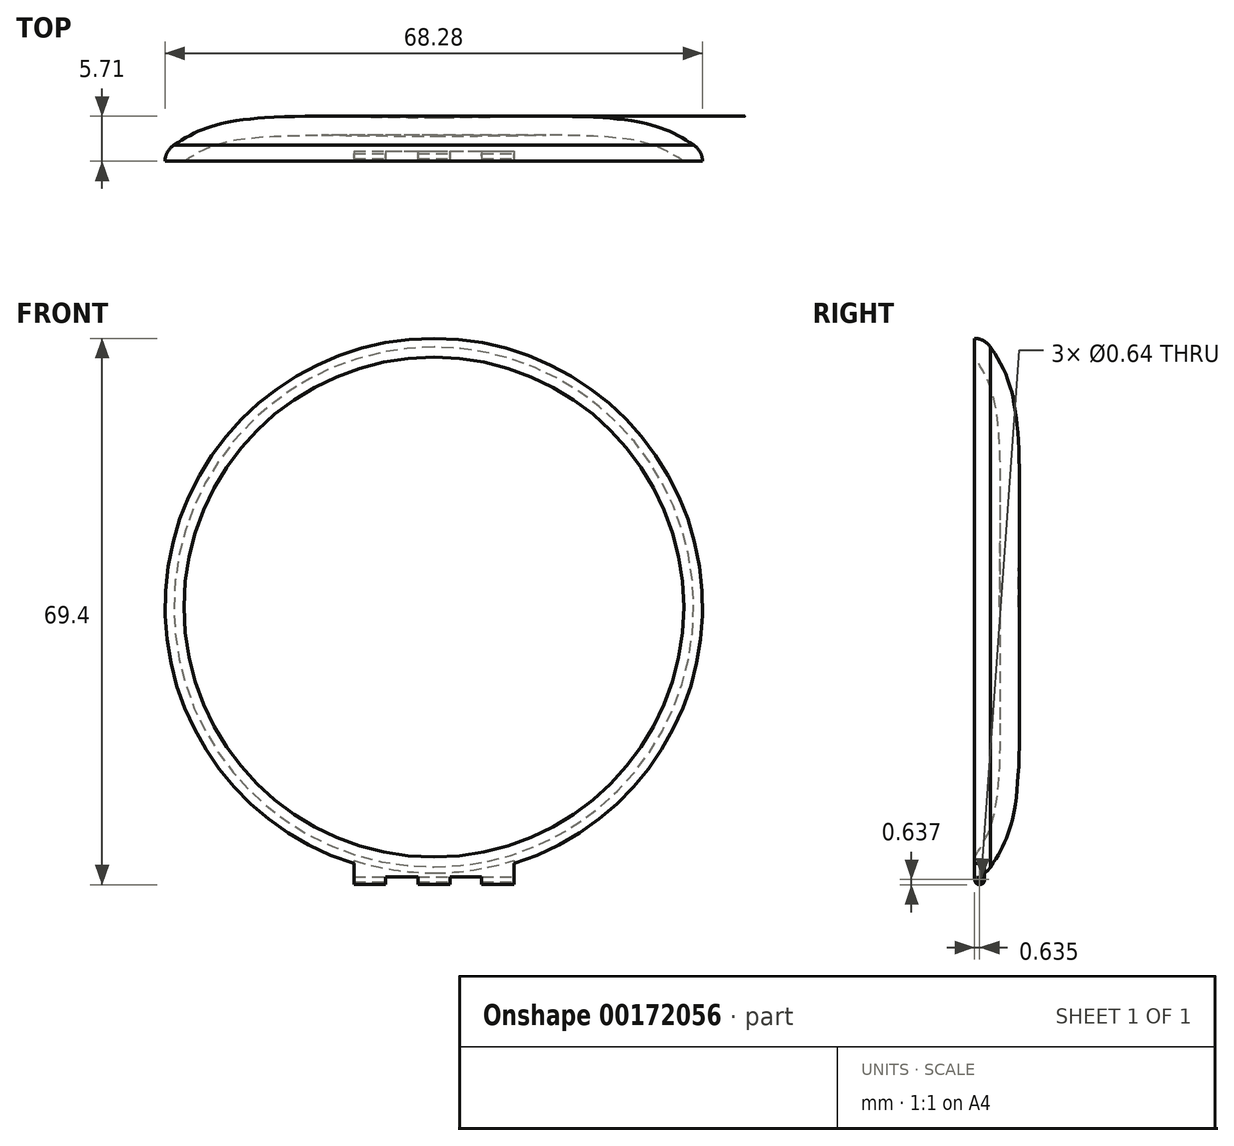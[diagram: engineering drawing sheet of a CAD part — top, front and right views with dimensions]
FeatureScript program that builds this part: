
annotation { "Feature Type Name" : "Feature", "Feature Type Description" : "" }
export const myFeature = defineFeature(function(context is Context, id is Id, definition is map)
    precondition{}
    {
        {
            var Q0;
            Q0=qCreatedBy(makeId("Right.planeOp"),FACE);
            var sketch = newSketch(context, id + "F0", { "sketchPlane" : qUnion([Q0])});
            skFitSpline(sketch, "E0", {"points": [v(3.18, 0) * mm, v(2.44, 26.5) * mm, v(0, 31.75) * mm], "startDerivative": vector(0, 46.41) * mm, "endDerivative": vector(-7.48, 11.96) * mm});
            skFitSpline(sketch, "E1.0", {"points": [v(5.56, 0) * mm, v(5.56, 1.92) * mm, v(5.6, 5.76) * mm, v(5.69, 11.37) * mm, v(5.7, 16.65) * mm, v(5.58, 20.62) * mm, v(5.36, 23.48) * mm, v(5.14, 25.12) * mm, v(4.92, 26.35) * mm, v(4.72, 27.23) * mm, v(4.5, 28.05) * mm, v(4.15, 29.07) * mm, v(3.68, 30.2) * mm, v(2.87, 31.7) * mm, v(2.31, 32.56) * mm, v(2.02, 33.02) * mm]});
            skLineSegment(sketch, "E2", {"start": v(3.18, 0) * mm, "end": v(5.56, 0) * mm});
            skArc(sketch, "E3", {"start": v(2.02, 33.02) * mm, "mid": v(1.16, 33.84) * mm, "end": v(0, 34.14) * mm});
            skLineSegment(sketch, "E4", {"start": v(0, 31.75) * mm, "end": v(0, 34.14) * mm});
            skSolve(sketch);
        }
        {
            var Q0;
            Q0 = qSketchRegion(id + "F0", true);
            var Q1;
            Q1=sQuery(id+"F0.wireOp",EDGE,"E2");
            revolve(context, id + "F1", {"entities" : qUnion([Q0]), "axis" : qUnion([Q1]), "revolveType" : RevolveType.FULL});
        }
        {
            var Q0;
            Q0=makeQuery(id+"F1.opRevolve","SWEPT_FACE",FACE,{"disambiguationData":[OSD([sQuery(id+"F0.wireOp",EDGE,"E4")])]});
            var sketch = newSketch(context, id + "F2", { "sketchPlane" : qUnion([Q0])});
            skLineSegment(sketch, "E5", {"start": v(0, 0) * mm, "end": v(0, -59.48) * mm, "construction": true});
            skArc(sketch, "E6", {"start": v(-10.16, -30.08) * mm, "mid": v(0, -31.75) * mm, "end": v(10.16, -30.08) * mm});
            skLineSegment(sketch, "E7", {"start": v(-10.16, -30.08) * mm, "end": v(-10.16, -35.26) * mm});
            skLineSegment(sketch, "E8", {"start": v(10.16, -30.08) * mm, "end": v(10.16, -35.26) * mm});
            skLineSegment(sketch, "E9", {"start": v(10.16, -35.26) * mm, "end": v(6.1, -35.26) * mm});
            skLineSegment(sketch, "E10", {"start": v(-2.03, -35.26) * mm, "end": v(-2.03, -34.25) * mm});
            skLineSegment(sketch, "E11", {"start": v(-6.1, -34.25) * mm, "end": v(-2.03, -34.25) * mm});
            skLineSegment(sketch, "E12", {"start": v(-6.1, -34.25) * mm, "end": v(-6.1, -35.26) * mm});
            skLineSegment(sketch, "E13", {"start": v(2.03, -35.26) * mm, "end": v(2.03, -34.25) * mm});
            skLineSegment(sketch, "E14", {"start": v(2.03, -34.25) * mm, "end": v(6.1, -34.25) * mm});
            skLineSegment(sketch, "E15", {"start": v(6.1, -34.25) * mm, "end": v(6.1, -35.26) * mm});
            skLineSegment(sketch, "E16.trimOffspring", {"start": v(-6.1, -35.26) * mm, "end": v(-10.16, -35.26) * mm});
            skLineSegment(sketch, "E17.trimOffspring", {"start": v(2.03, -35.26) * mm, "end": v(-2.03, -35.26) * mm});
            skLineSegment(sketch, "E18", {"start": v(-2.03, -34.25) * mm, "end": v(2.03, -34.25) * mm, "construction": true});
            skSolve(sketch);
        }
        {
            var Q0;
            Q0 = qSketchRegion(id + "F2", true);
            extrude(context, id + "F3", {"entities" : qUnion([Q0]), "operationType" : NewBodyOperationType.ADD, "oppositeDirection" : true, "depth" : 1.27 * mm});
        }
        {
            var Q0;
            Q0=makeQuery(id+"F3.opExtrude","SWEPT_FACE",FACE,{"disambiguationData":[OSD([sQuery(id+"F2.wireOp",EDGE,"E8")])]});
            var sketch = newSketch(context, id + "F4", { "sketchPlane" : qUnion([Q0])});
            skCircle(sketch, "E19", {"center": v(0.64, -34.62) * mm, "radius": 0.32 * mm});
            skLineSegment(sketch, "E20", {"start": v(1.86, -34.62) * mm, "end": v(-1.09, -34.62) * mm, "construction": true});
            skArc(sketch, "E21", {"start": v(0, -34.62) * mm, "mid": v(0.64, -35.26) * mm, "end": v(1.27, -34.62) * mm});
            skLineSegment(sketch, "E22", {"start": v(0, -34.62) * mm, "end": v(0, -35.26) * mm});
            skLineSegment(sketch, "E23", {"start": v(0, -35.26) * mm, "end": v(1.27, -35.26) * mm});
            skLineSegment(sketch, "E24", {"start": v(1.27, -35.26) * mm, "end": v(1.27, -34.62) * mm});
            skSolve(sketch);
        }
        {
            var Q0;
            Q0 = qSketchRegion(id + "F4", true);
            extrude(context, id + "F5", {"entities" : qUnion([Q0]), "operationType" : NewBodyOperationType.REMOVE, "endBound" : BoundingType.THROUGH_ALL, "oppositeDirection" : true, "depth" : 25.4 * mm});
        }
    });
